# Revit family: Sink-Vessel_Lavatory-KOHLER-Carillon-K-75748
name_source: partatom
category: Plumbing Fixtures
revit_build: Autodesk Revit 2015 (Build: 20140606_1530(x64)
units: mm (PartAtom-declared; Revit-internal decimal feet)

## types (4) — shared parameters
ADA Compliant = Yes
Assembly Code = D2010400
CW Connection = No
Cold Water Inlet = Cold Water Inlet
Date Modified = 01/10/2019
Default Elevation = 36"
Drain Included = No
HW Connection = No
Height = 6"
Hot Water Inlet = Hot Water Inlet
Length = 17 11/16"
Manufacturer = KOHLER Co.
MasterFormat 1995 = 15410
MasterFormat 2004 = 22.41.16
Material = Vitreous China
Product Documentation Link = http://www.us.kohler.com
Product Name = Carillon
Product Page URL = http://www.us.kohler.com
URL = https://www.us.kohler.com
Vent Connection = No
Waste Connection = Yes
Waste Water Outlet = Waste Water Outlet
Width = 17 11/16"

## per-type parameters (varying)
| type | Description | Finish | Model | Type |
| Sartorial Herringbone, 0-White | Sartorial Herringbone in White on Carillon Round Wading Pool bathroom sink | Kohler-Vitreous_China-0-White | K-75748-HD1-0 | 1 |
| Sartorial Herringbone, 7-Black Black | Sartorial Herringbone in Black Black on Carillon Round Wading Pool bathroom sink | Kohler-Vitreous_China-7-Black_Black | K-75748-HD2-7 | 2 |
| Sartorial Paisley, 0-White | Sartorial Paisley in White on Carillon Round Wading Pool bathroom sink | Kohler-Vitreous_China-0-White | K-75748-FP1-0 | 3 |
| Sartorial Paisley, 7-Black Black | Sartorial Paisley in Black Black on Carillon Round Wading Pool bathroom sink | Kohler-Vitreous_China-7-Black_Black | K-75748-FP2-7 | 4 |

## geometry (parser evidence)
native form markers: Sweep x6
no freeform markers — native parametric forms only
